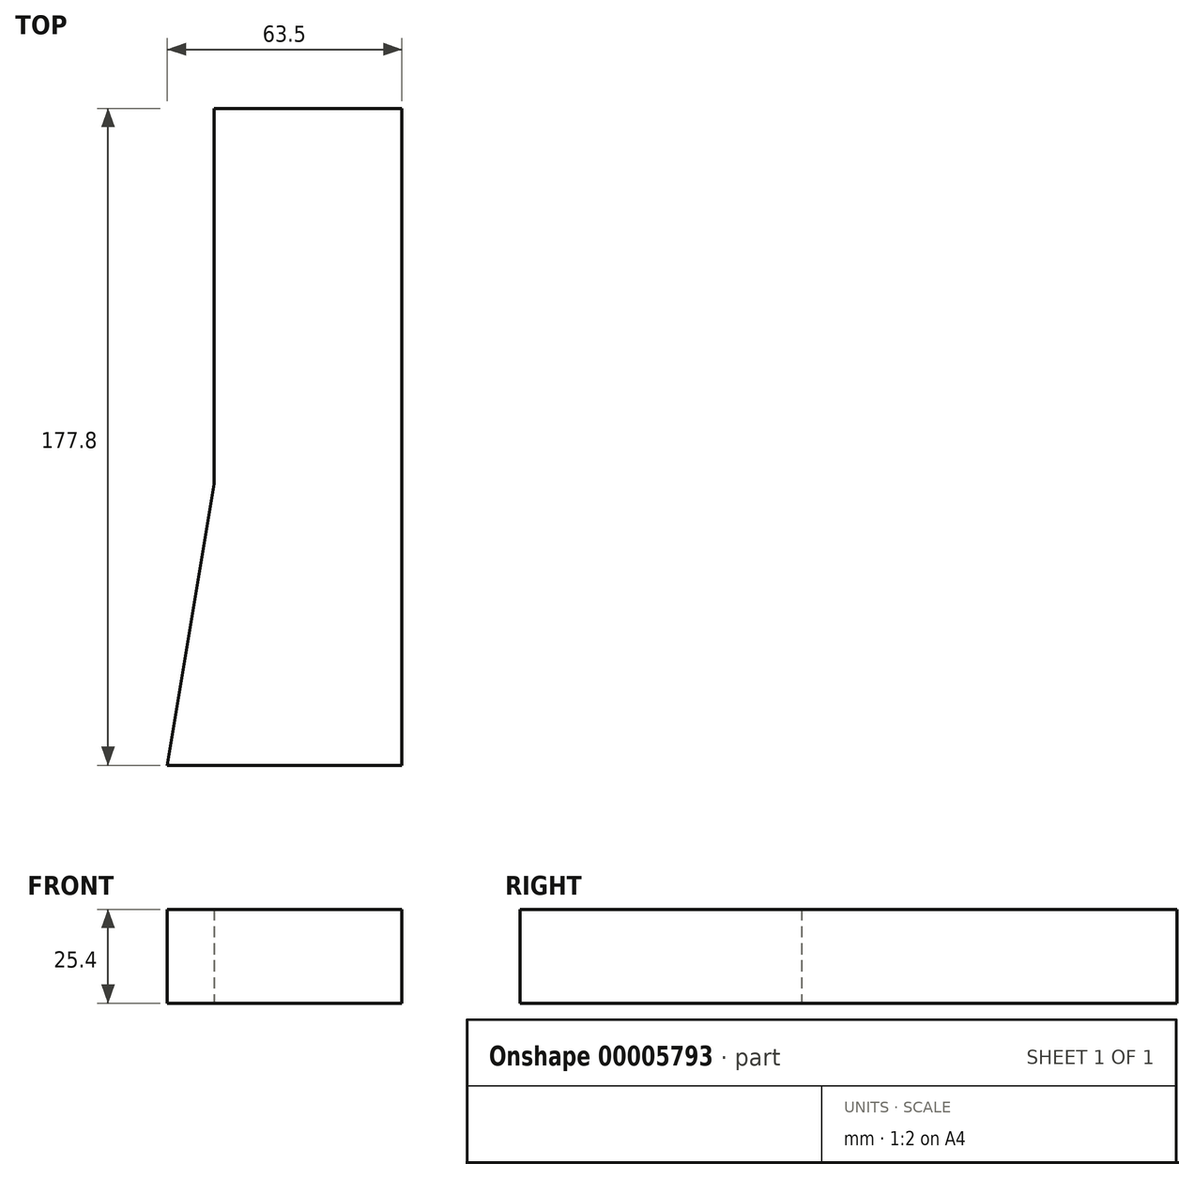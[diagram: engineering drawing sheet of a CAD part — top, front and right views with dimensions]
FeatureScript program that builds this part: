
annotation { "Feature Type Name" : "Feature", "Feature Type Description" : "" }
export const myFeature = defineFeature(function(context is Context, id is Id, definition is map)
    precondition{}
    {
        {
            var Q0;
            Q0=qCreatedBy(makeId("Top.planeOp"),FACE);
            var sketch = newSketch(context, id + "F0", { "sketchPlane" : qUnion([Q0])});
            skLineSegment(sketch, "E0", {"start": v(-63.5, 0) * mm, "end": v(-50.8, 76.2) * mm});
            skLineSegment(sketch, "E1", {"start": v(-50.8, 76.2) * mm, "end": v(-50.8, 177.8) * mm});
            skLineSegment(sketch, "E2", {"start": v(-50.8, 177.8) * mm, "end": v(0, 177.8) * mm});
            skLineSegment(sketch, "E3", {"start": v(0, 177.8) * mm, "end": v(0, 76.2) * mm});
            skLineSegment(sketch, "E4", {"start": v(0, 76.2) * mm, "end": v(0, 0) * mm});
            skLineSegment(sketch, "E5", {"start": v(0, 0) * mm, "end": v(-63.5, 0) * mm});
            skSolve(sketch);
        }
        {
            var Q0;
            Q0=makeQuery(id+"F0.imprint","IMPRINT",FACE,{"disambiguationData":[TD([[makeQuery(id+"F0.imprint","IMPRINT",EDGE,{"derivedFrom":sQuery(id+"F0.wireOp",EDGE,"E0")}),-1.0]])]});
            extrude(context, id + "F1", {"entities" : qUnion([Q0]), "depth" : 25.4 * mm});
        }
    });
